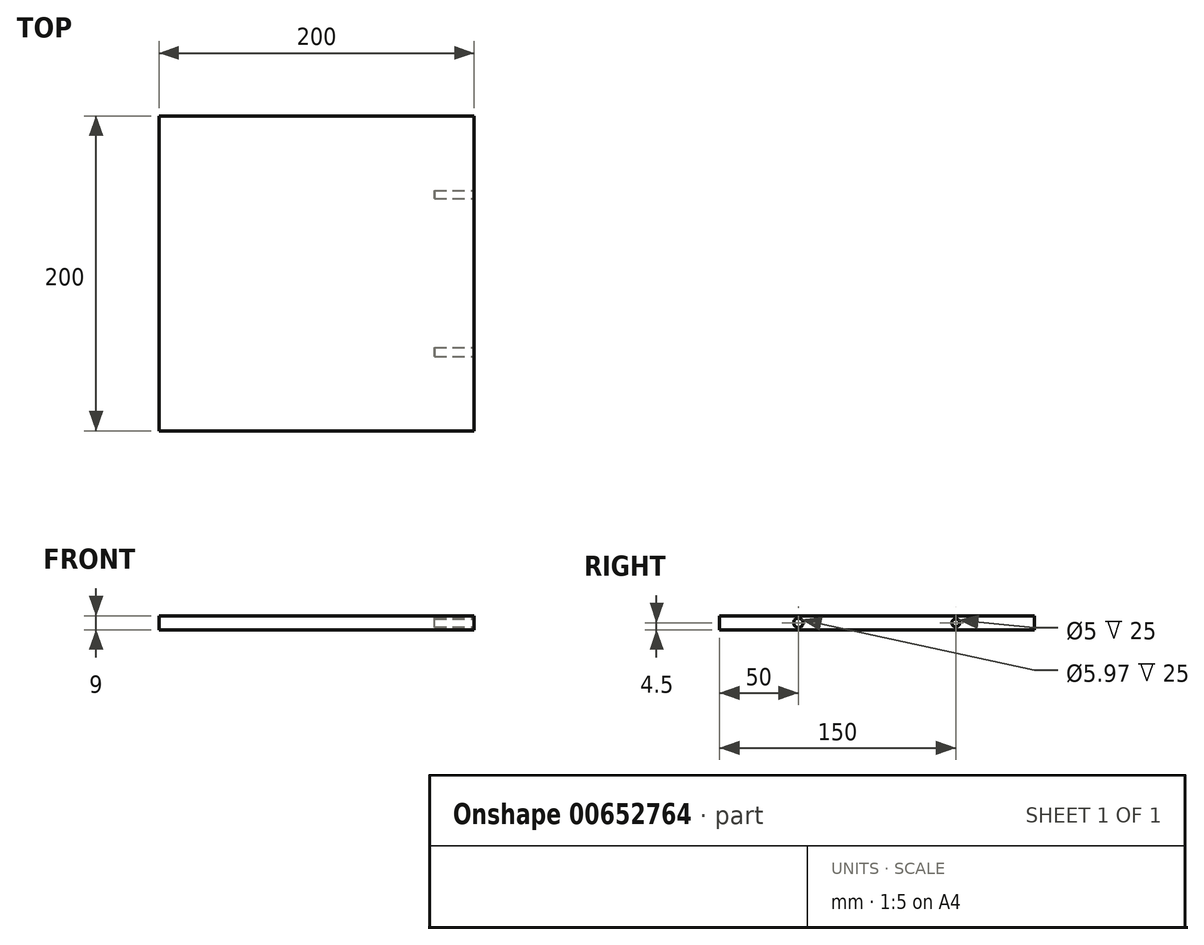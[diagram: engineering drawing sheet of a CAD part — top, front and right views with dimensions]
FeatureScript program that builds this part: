
annotation { "Feature Type Name" : "Feature", "Feature Type Description" : "" }
export const myFeature = defineFeature(function(context is Context, id is Id, definition is map)
    precondition{}
    {
        {
            var Q0;
            Q0=qCreatedBy(makeId("Top.planeOp"),FACE);
            var sketch = newSketch(context, id + "F0", { "sketchPlane" : qUnion([Q0])});
            skLineSegment(sketch, "E0.bottom", {"start": v(-100, 100) * mm, "end": v(100, 100) * mm});
            skLineSegment(sketch, "E0.top", {"start": v(-100, -100) * mm, "end": v(100, -100) * mm});
            skLineSegment(sketch, "E0.left", {"start": v(-100, 100) * mm, "end": v(-100, -100) * mm});
            skLineSegment(sketch, "E0.right", {"start": v(100, 100) * mm, "end": v(100, -100) * mm});
            skPoint(sketch, "E0.middle", {"position": v(0, 0) * mm});
            skSolve(sketch);
        }
        {
            var Q0;
            Q0=makeQuery(id+"F0.imprint","IMPRINT",FACE,{"disambiguationData":[TD([[makeQuery(id+"F0.imprint","IMPRINT",EDGE,{"derivedFrom":sQuery(id+"F0.wireOp",EDGE,"E0.bottom")}),-1.0]])]});
            extrude(context, id + "F1", {"entities" : qUnion([Q0]), "depth" : 9 * mm, "offsetDistance" : 25 * mm});
        }
        {
            var Q0;
            Q0=makeQuery(id+"F1.opExtrude","SWEPT_FACE",FACE,{"disambiguationData":[OSD([sQuery(id+"F0.wireOp",EDGE,"E0.right")])]});
            var sketch = newSketch(context, id + "F2", { "sketchPlane" : qUnion([Q0])});
            skCircle(sketch, "E1", {"center": v(-50, 4.5) * mm, "radius": 2.98 * mm});
            skCircle(sketch, "E2", {"center": v(50, 4.5) * mm, "radius": 2.5 * mm});
            skSolve(sketch);
        }
        {
            var Q0;
            Q0 = qSketchRegion(id + "F2", true);
            extrude(context, id + "F3", {"entities" : qUnion([Q0]), "operationType" : NewBodyOperationType.REMOVE, "oppositeDirection" : true, "depth" : 25 * mm, "offsetDistance" : 25 * mm});
        }
        {
            var Q0;
            Q0=makeQuery(id+"F2.imprint","IMPRINT",FACE,{"disambiguationData":[TD([[makeQuery(id+"F2.imprint","IMPRINT",EDGE,{"derivedFrom":sQuery(id+"F2.wireOp",EDGE,"E1")}),1.0]])]});
            extrude(context, id + "F4", {"entities" : qUnion([Q0]), "operationType" : NewBodyOperationType.REMOVE, "oppositeDirection" : true, "depth" : 15 * mm, "offsetDistance" : 25 * mm});
        }
    });
